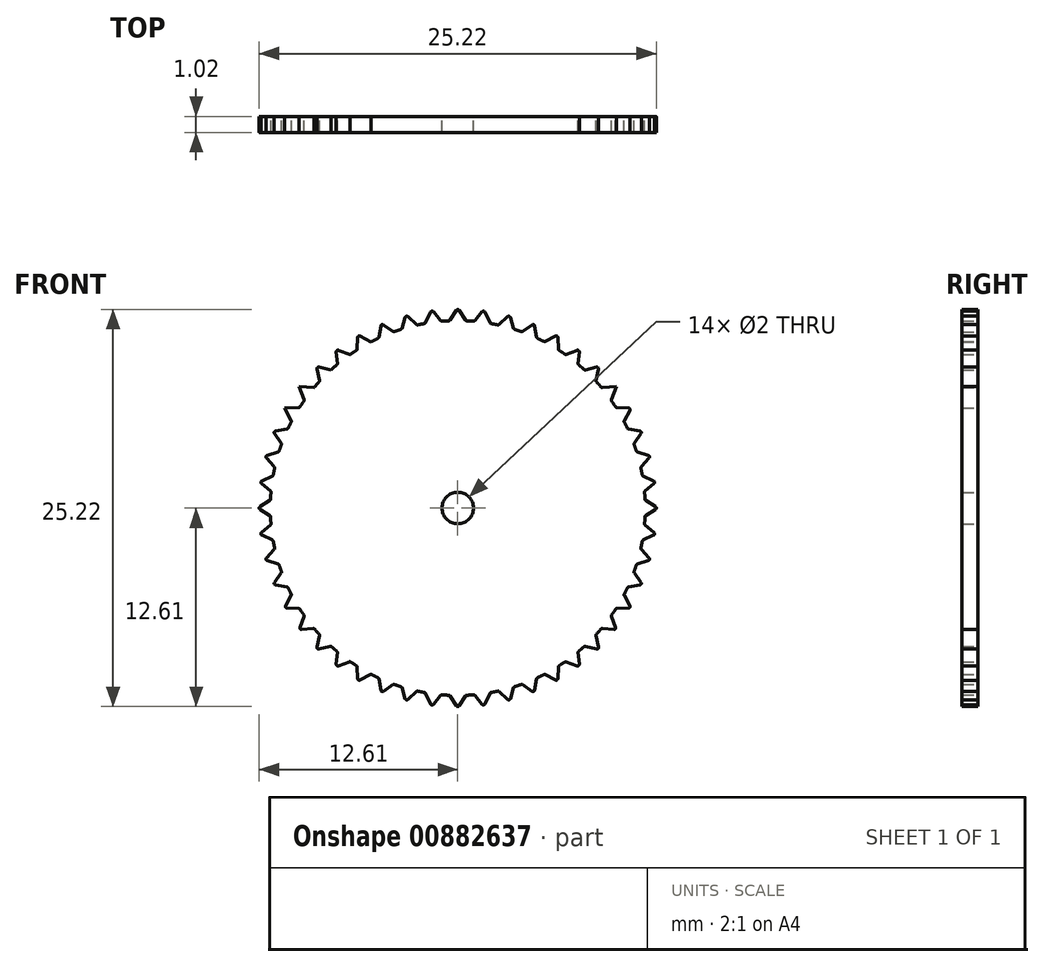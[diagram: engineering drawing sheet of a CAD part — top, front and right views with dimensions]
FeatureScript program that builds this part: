
annotation { "Feature Type Name" : "Feature", "Feature Type Description" : "" }
export const myFeature = defineFeature(function(context is Context, id is Id, definition is map)
    precondition{}
    {
        {
            var Q0;
            Q0=qCreatedBy(makeId("Front.planeOp"),FACE);
            var sketch = newSketch(context, id + "F0", { "sketchPlane" : qUnion([Q0])});
            skArc(sketch, "E0", {"start": v(-0.5, 11.9) * mm, "mid": v(0, -11.9) * mm, "end": v(0.5, 11.9) * mm});
            skLineSegment(sketch, "E1", {"start": v(-0.5, 11.9) * mm, "end": v(0, 12.7) * mm});
            skLineSegment(sketch, "E2", {"start": v(0, 12.7) * mm, "end": v(0.5, 11.9) * mm});
            skPoint(sketch, "E3.start.orphan", {"position": v(-0.5, 15.6) * mm});
            skPoint(sketch, "E4.end.orphan", {"position": v(0, 15.6) * mm});
            skCircle(sketch, "E5", {"center": v(0, 0) * mm, "radius": 1 * mm});
            skPoint(sketch, "E6.end.orphan", {"position": v(0, 11.9) * mm});
            skLineSegment(sketch, "E7.1.0", {"start": v(-2.06, 11.73) * mm, "end": v(-1.66, 12.6) * mm});
            skLineSegment(sketch, "E7.1.1", {"start": v(-1.66, 12.6) * mm, "end": v(-1.05, 11.86) * mm});
            skLineSegment(sketch, "E7.2.0", {"start": v(-3.57, 11.36) * mm, "end": v(-3.29, 12.27) * mm});
            skLineSegment(sketch, "E7.2.1", {"start": v(-3.29, 12.27) * mm, "end": v(-2.59, 11.62) * mm});
            skLineSegment(sketch, "E7.3.0", {"start": v(-5.02, 10.8) * mm, "end": v(-4.86, 11.73) * mm});
            skLineSegment(sketch, "E7.3.1", {"start": v(-4.86, 11.73) * mm, "end": v(-4.08, 11.18) * mm});
            skLineSegment(sketch, "E7.4.0", {"start": v(-6.39, 10.05) * mm, "end": v(-6.35, 11) * mm});
            skLineSegment(sketch, "E7.4.1", {"start": v(-6.35, 11) * mm, "end": v(-5.5, 10.56) * mm});
            skLineSegment(sketch, "E7.5.0", {"start": v(-7.64, 9.13) * mm, "end": v(-7.73, 10.08) * mm});
            skLineSegment(sketch, "E7.5.1", {"start": v(-7.73, 10.08) * mm, "end": v(-6.84, 9.75) * mm});
            skLineSegment(sketch, "E7.6.0", {"start": v(-8.77, 8.05) * mm, "end": v(-8.98, 8.98) * mm});
            skLineSegment(sketch, "E7.6.1", {"start": v(-8.98, 8.98) * mm, "end": v(-8.05, 8.77) * mm});
            skLineSegment(sketch, "E7.7.0", {"start": v(-9.75, 6.84) * mm, "end": v(-10.08, 7.73) * mm});
            skLineSegment(sketch, "E7.7.1", {"start": v(-10.08, 7.73) * mm, "end": v(-9.13, 7.64) * mm});
            skLineSegment(sketch, "E7.8.0", {"start": v(-10.56, 5.5) * mm, "end": v(-11, 6.35) * mm});
            skLineSegment(sketch, "E7.8.1", {"start": v(-11, 6.35) * mm, "end": v(-10.05, 6.39) * mm});
            skLineSegment(sketch, "E7.9.0", {"start": v(-11.18, 4.08) * mm, "end": v(-11.73, 4.86) * mm});
            skLineSegment(sketch, "E7.9.1", {"start": v(-11.73, 4.86) * mm, "end": v(-10.8, 5.02) * mm});
            skLineSegment(sketch, "E7.10.0", {"start": v(-11.62, 2.59) * mm, "end": v(-12.27, 3.29) * mm});
            skLineSegment(sketch, "E7.10.1", {"start": v(-12.27, 3.29) * mm, "end": v(-11.36, 3.57) * mm});
            skLineSegment(sketch, "E7.11.0", {"start": v(-11.86, 1.05) * mm, "end": v(-12.6, 1.66) * mm});
            skLineSegment(sketch, "E7.11.1", {"start": v(-12.6, 1.66) * mm, "end": v(-11.73, 2.06) * mm});
            skLineSegment(sketch, "E7.12.0", {"start": v(-11.9, -0.5) * mm, "end": v(-12.7, 0) * mm});
            skLineSegment(sketch, "E7.12.1", {"start": v(-12.7, 0) * mm, "end": v(-11.9, 0.5) * mm});
            skLineSegment(sketch, "E7.13.0", {"start": v(-11.73, -2.06) * mm, "end": v(-12.6, -1.66) * mm});
            skLineSegment(sketch, "E7.13.1", {"start": v(-12.6, -1.66) * mm, "end": v(-11.86, -1.05) * mm});
            skLineSegment(sketch, "E7.14.0", {"start": v(-11.36, -3.57) * mm, "end": v(-12.27, -3.29) * mm});
            skLineSegment(sketch, "E7.14.1", {"start": v(-12.27, -3.29) * mm, "end": v(-11.62, -2.59) * mm});
            skLineSegment(sketch, "E7.15.0", {"start": v(-10.8, -5.02) * mm, "end": v(-11.73, -4.86) * mm});
            skLineSegment(sketch, "E7.15.1", {"start": v(-11.73, -4.86) * mm, "end": v(-11.18, -4.08) * mm});
            skLineSegment(sketch, "E7.16.0", {"start": v(-10.05, -6.39) * mm, "end": v(-11, -6.35) * mm});
            skLineSegment(sketch, "E7.16.1", {"start": v(-11, -6.35) * mm, "end": v(-10.56, -5.5) * mm});
            skLineSegment(sketch, "E7.17.0", {"start": v(-9.13, -7.64) * mm, "end": v(-10.08, -7.73) * mm});
            skLineSegment(sketch, "E7.17.1", {"start": v(-10.08, -7.73) * mm, "end": v(-9.75, -6.84) * mm});
            skLineSegment(sketch, "E7.18.0", {"start": v(-8.05, -8.77) * mm, "end": v(-8.98, -8.98) * mm});
            skLineSegment(sketch, "E7.18.1", {"start": v(-8.98, -8.98) * mm, "end": v(-8.77, -8.05) * mm});
            skLineSegment(sketch, "E7.19.0", {"start": v(-6.84, -9.75) * mm, "end": v(-7.73, -10.08) * mm});
            skLineSegment(sketch, "E7.19.1", {"start": v(-7.73, -10.08) * mm, "end": v(-7.64, -9.13) * mm});
            skLineSegment(sketch, "E7.20.0", {"start": v(-5.5, -10.56) * mm, "end": v(-6.35, -11) * mm});
            skLineSegment(sketch, "E7.20.1", {"start": v(-6.35, -11) * mm, "end": v(-6.39, -10.05) * mm});
            skLineSegment(sketch, "E7.21.0", {"start": v(-4.08, -11.18) * mm, "end": v(-4.86, -11.73) * mm});
            skLineSegment(sketch, "E7.21.1", {"start": v(-4.86, -11.73) * mm, "end": v(-5.02, -10.8) * mm});
            skLineSegment(sketch, "E7.22.0", {"start": v(-2.59, -11.62) * mm, "end": v(-3.29, -12.27) * mm});
            skLineSegment(sketch, "E7.22.1", {"start": v(-3.29, -12.27) * mm, "end": v(-3.57, -11.36) * mm});
            skLineSegment(sketch, "E7.23.0", {"start": v(-1.05, -11.86) * mm, "end": v(-1.66, -12.6) * mm});
            skLineSegment(sketch, "E7.23.1", {"start": v(-1.66, -12.6) * mm, "end": v(-2.06, -11.73) * mm});
            skLineSegment(sketch, "E7.24.0", {"start": v(0.5, -11.9) * mm, "end": v(0, -12.7) * mm});
            skLineSegment(sketch, "E7.24.1", {"start": v(0, -12.7) * mm, "end": v(-0.5, -11.9) * mm});
            skLineSegment(sketch, "E7.25.0", {"start": v(2.06, -11.73) * mm, "end": v(1.66, -12.6) * mm});
            skLineSegment(sketch, "E7.25.1", {"start": v(1.66, -12.6) * mm, "end": v(1.05, -11.86) * mm});
            skLineSegment(sketch, "E7.26.0", {"start": v(3.57, -11.36) * mm, "end": v(3.29, -12.27) * mm});
            skLineSegment(sketch, "E7.26.1", {"start": v(3.29, -12.27) * mm, "end": v(2.59, -11.62) * mm});
            skLineSegment(sketch, "E7.27.0", {"start": v(5.02, -10.8) * mm, "end": v(4.86, -11.73) * mm});
            skLineSegment(sketch, "E7.27.1", {"start": v(4.86, -11.73) * mm, "end": v(4.08, -11.18) * mm});
            skLineSegment(sketch, "E7.28.0", {"start": v(6.39, -10.05) * mm, "end": v(6.35, -11) * mm});
            skLineSegment(sketch, "E7.28.1", {"start": v(6.35, -11) * mm, "end": v(5.5, -10.56) * mm});
            skLineSegment(sketch, "E7.29.0", {"start": v(7.64, -9.13) * mm, "end": v(7.73, -10.08) * mm});
            skLineSegment(sketch, "E7.29.1", {"start": v(7.73, -10.08) * mm, "end": v(6.84, -9.75) * mm});
            skLineSegment(sketch, "E7.30.0", {"start": v(8.77, -8.05) * mm, "end": v(8.98, -8.98) * mm});
            skLineSegment(sketch, "E7.30.1", {"start": v(8.98, -8.98) * mm, "end": v(8.05, -8.77) * mm});
            skLineSegment(sketch, "E7.31.0", {"start": v(9.75, -6.84) * mm, "end": v(10.08, -7.73) * mm});
            skLineSegment(sketch, "E7.31.1", {"start": v(10.08, -7.73) * mm, "end": v(9.13, -7.64) * mm});
            skLineSegment(sketch, "E7.32.0", {"start": v(10.56, -5.5) * mm, "end": v(11, -6.35) * mm});
            skLineSegment(sketch, "E7.32.1", {"start": v(11, -6.35) * mm, "end": v(10.05, -6.39) * mm});
            skLineSegment(sketch, "E7.33.0", {"start": v(11.18, -4.08) * mm, "end": v(11.73, -4.86) * mm});
            skLineSegment(sketch, "E7.33.1", {"start": v(11.73, -4.86) * mm, "end": v(10.8, -5.02) * mm});
            skLineSegment(sketch, "E7.34.0", {"start": v(11.62, -2.59) * mm, "end": v(12.27, -3.29) * mm});
            skLineSegment(sketch, "E7.34.1", {"start": v(12.27, -3.29) * mm, "end": v(11.36, -3.57) * mm});
            skLineSegment(sketch, "E7.35.0", {"start": v(11.86, -1.05) * mm, "end": v(12.6, -1.66) * mm});
            skLineSegment(sketch, "E7.35.1", {"start": v(12.6, -1.66) * mm, "end": v(11.73, -2.06) * mm});
            skLineSegment(sketch, "E7.36.0", {"start": v(11.9, 0.5) * mm, "end": v(12.7, 0) * mm});
            skLineSegment(sketch, "E7.36.1", {"start": v(12.7, 0) * mm, "end": v(11.9, -0.5) * mm});
            skLineSegment(sketch, "E7.37.0", {"start": v(11.73, 2.06) * mm, "end": v(12.6, 1.66) * mm});
            skLineSegment(sketch, "E7.37.1", {"start": v(12.6, 1.66) * mm, "end": v(11.86, 1.05) * mm});
            skLineSegment(sketch, "E7.38.0", {"start": v(11.36, 3.57) * mm, "end": v(12.27, 3.29) * mm});
            skLineSegment(sketch, "E7.38.1", {"start": v(12.27, 3.29) * mm, "end": v(11.62, 2.59) * mm});
            skLineSegment(sketch, "E7.39.0", {"start": v(10.8, 5.02) * mm, "end": v(11.73, 4.86) * mm});
            skLineSegment(sketch, "E7.39.1", {"start": v(11.73, 4.86) * mm, "end": v(11.18, 4.08) * mm});
            skLineSegment(sketch, "E7.40.0", {"start": v(10.05, 6.39) * mm, "end": v(11, 6.35) * mm});
            skLineSegment(sketch, "E7.40.1", {"start": v(11, 6.35) * mm, "end": v(10.56, 5.5) * mm});
            skLineSegment(sketch, "E7.41.0", {"start": v(9.13, 7.64) * mm, "end": v(10.08, 7.73) * mm});
            skLineSegment(sketch, "E7.41.1", {"start": v(10.08, 7.73) * mm, "end": v(9.75, 6.84) * mm});
            skLineSegment(sketch, "E7.42.0", {"start": v(8.05, 8.77) * mm, "end": v(8.98, 8.98) * mm});
            skLineSegment(sketch, "E7.42.1", {"start": v(8.98, 8.98) * mm, "end": v(8.77, 8.05) * mm});
            skLineSegment(sketch, "E7.43.0", {"start": v(6.84, 9.75) * mm, "end": v(7.73, 10.08) * mm});
            skLineSegment(sketch, "E7.43.1", {"start": v(7.73, 10.08) * mm, "end": v(7.64, 9.13) * mm});
            skLineSegment(sketch, "E7.44.0", {"start": v(5.5, 10.56) * mm, "end": v(6.35, 11) * mm});
            skLineSegment(sketch, "E7.44.1", {"start": v(6.35, 11) * mm, "end": v(6.39, 10.05) * mm});
            skLineSegment(sketch, "E7.45.0", {"start": v(4.08, 11.18) * mm, "end": v(4.86, 11.73) * mm});
            skLineSegment(sketch, "E7.45.1", {"start": v(4.86, 11.73) * mm, "end": v(5.02, 10.8) * mm});
            skLineSegment(sketch, "E7.46.0", {"start": v(2.59, 11.62) * mm, "end": v(3.29, 12.27) * mm});
            skLineSegment(sketch, "E7.46.1", {"start": v(3.29, 12.27) * mm, "end": v(3.57, 11.36) * mm});
            skLineSegment(sketch, "E7.47.0", {"start": v(1.05, 11.86) * mm, "end": v(1.66, 12.6) * mm});
            skLineSegment(sketch, "E7.47.1", {"start": v(1.66, 12.6) * mm, "end": v(2.06, 11.73) * mm});
            skSolve(sketch);
        }
        {
            var Q0;
            {var subQ0=sQuery(id+"F0.wireOp",EDGE,"E1");Q0=makeQuery(id+"F0.imprint","IMPRINT",FACE,{"disambiguationData":[TD([[makeQuery(id+"F0.imprint","IMPRINT",EDGE,{"derivedFrom":subQ0}),-1.0]])]});}
            var Q1;
            {var subQ0=sQuery(id+"F0.wireOp",EDGE,"E7.1.0");Q1=makeQuery(id+"F0.imprint","IMPRINT",FACE,{"disambiguationData":[TD([[makeQuery(id+"F0.imprint","IMPRINT",EDGE,{"derivedFrom":subQ0}),-1.0]])]});}
            var Q2;
            {var subQ0=sQuery(id+"F0.wireOp",EDGE,"E7.2.0");Q2=makeQuery(id+"F0.imprint","IMPRINT",FACE,{"disambiguationData":[TD([[makeQuery(id+"F0.imprint","IMPRINT",EDGE,{"derivedFrom":subQ0}),-1.0]])]});}
            var Q3;
            {var subQ0=sQuery(id+"F0.wireOp",EDGE,"E7.3.0");Q3=makeQuery(id+"F0.imprint","IMPRINT",FACE,{"disambiguationData":[TD([[makeQuery(id+"F0.imprint","IMPRINT",EDGE,{"derivedFrom":subQ0}),-1.0]])]});}
            var Q4;
            {var subQ0=sQuery(id+"F0.wireOp",EDGE,"E7.4.0");Q4=makeQuery(id+"F0.imprint","IMPRINT",FACE,{"disambiguationData":[TD([[makeQuery(id+"F0.imprint","IMPRINT",EDGE,{"derivedFrom":subQ0}),-1.0]])]});}
            var Q5;
            {var subQ0=sQuery(id+"F0.wireOp",EDGE,"E7.5.0");Q5=makeQuery(id+"F0.imprint","IMPRINT",FACE,{"disambiguationData":[TD([[makeQuery(id+"F0.imprint","IMPRINT",EDGE,{"derivedFrom":subQ0}),-1.0]])]});}
            var Q6;
            {var subQ0=sQuery(id+"F0.wireOp",EDGE,"E7.6.0");Q6=makeQuery(id+"F0.imprint","IMPRINT",FACE,{"disambiguationData":[TD([[makeQuery(id+"F0.imprint","IMPRINT",EDGE,{"derivedFrom":subQ0}),-1.0]])]});}
            var Q7;
            {var subQ0=sQuery(id+"F0.wireOp",EDGE,"E7.8.0");Q7=makeQuery(id+"F0.imprint","IMPRINT",FACE,{"disambiguationData":[TD([[makeQuery(id+"F0.imprint","IMPRINT",EDGE,{"derivedFrom":subQ0}),-1.0]])]});}
            var Q8;
            {var subQ0=sQuery(id+"F0.wireOp",EDGE,"E7.9.0");Q8=makeQuery(id+"F0.imprint","IMPRINT",FACE,{"disambiguationData":[TD([[makeQuery(id+"F0.imprint","IMPRINT",EDGE,{"derivedFrom":subQ0}),-1.0]])]});}
            var Q9;
            {var subQ0=sQuery(id+"F0.wireOp",EDGE,"E7.10.0");Q9=makeQuery(id+"F0.imprint","IMPRINT",FACE,{"disambiguationData":[TD([[makeQuery(id+"F0.imprint","IMPRINT",EDGE,{"derivedFrom":subQ0}),-1.0]])]});}
            var Q10;
            {var subQ0=sQuery(id+"F0.wireOp",EDGE,"E7.11.0");Q10=makeQuery(id+"F0.imprint","IMPRINT",FACE,{"disambiguationData":[TD([[makeQuery(id+"F0.imprint","IMPRINT",EDGE,{"derivedFrom":subQ0}),-1.0]])]});}
            var Q11;
            {var subQ0=sQuery(id+"F0.wireOp",EDGE,"E7.12.0");Q11=makeQuery(id+"F0.imprint","IMPRINT",FACE,{"disambiguationData":[TD([[makeQuery(id+"F0.imprint","IMPRINT",EDGE,{"derivedFrom":subQ0}),-1.0]])]});}
            var Q12;
            {var subQ0=sQuery(id+"F0.wireOp",EDGE,"E7.13.0");Q12=makeQuery(id+"F0.imprint","IMPRINT",FACE,{"disambiguationData":[TD([[makeQuery(id+"F0.imprint","IMPRINT",EDGE,{"derivedFrom":subQ0}),-1.0]])]});}
            var Q13;
            {var subQ0=sQuery(id+"F0.wireOp",EDGE,"E7.7.0");Q13=makeQuery(id+"F0.imprint","IMPRINT",FACE,{"disambiguationData":[TD([[makeQuery(id+"F0.imprint","IMPRINT",EDGE,{"derivedFrom":subQ0}),-1.0]])]});}
            var Q14;
            {var subQ0=sQuery(id+"F0.wireOp",EDGE,"E7.14.0");Q14=makeQuery(id+"F0.imprint","IMPRINT",FACE,{"disambiguationData":[TD([[makeQuery(id+"F0.imprint","IMPRINT",EDGE,{"derivedFrom":subQ0}),-1.0]])]});}
            var Q15;
            {var subQ0=sQuery(id+"F0.wireOp",EDGE,"E7.15.0");Q15=makeQuery(id+"F0.imprint","IMPRINT",FACE,{"disambiguationData":[TD([[makeQuery(id+"F0.imprint","IMPRINT",EDGE,{"derivedFrom":subQ0}),-1.0]])]});}
            var Q16;
            {var subQ0=sQuery(id+"F0.wireOp",EDGE,"E7.16.0");Q16=makeQuery(id+"F0.imprint","IMPRINT",FACE,{"disambiguationData":[TD([[makeQuery(id+"F0.imprint","IMPRINT",EDGE,{"derivedFrom":subQ0}),-1.0]])]});}
            var Q17;
            {var subQ0=sQuery(id+"F0.wireOp",EDGE,"E7.47.0");Q17=makeQuery(id+"F0.imprint","IMPRINT",FACE,{"disambiguationData":[TD([[makeQuery(id+"F0.imprint","IMPRINT",EDGE,{"derivedFrom":subQ0}),-1.0]])]});}
            var Q18;
            {var subQ0=sQuery(id+"F0.wireOp",EDGE,"E7.46.0");Q18=makeQuery(id+"F0.imprint","IMPRINT",FACE,{"disambiguationData":[TD([[makeQuery(id+"F0.imprint","IMPRINT",EDGE,{"derivedFrom":subQ0}),-1.0]])]});}
            var Q19;
            {var subQ0=sQuery(id+"F0.wireOp",EDGE,"E7.45.0");Q19=makeQuery(id+"F0.imprint","IMPRINT",FACE,{"disambiguationData":[TD([[makeQuery(id+"F0.imprint","IMPRINT",EDGE,{"derivedFrom":subQ0}),-1.0]])]});}
            var Q20;
            {var subQ0=sQuery(id+"F0.wireOp",EDGE,"E7.44.0");Q20=makeQuery(id+"F0.imprint","IMPRINT",FACE,{"disambiguationData":[TD([[makeQuery(id+"F0.imprint","IMPRINT",EDGE,{"derivedFrom":subQ0}),-1.0]])]});}
            var Q21;
            {var subQ0=sQuery(id+"F0.wireOp",EDGE,"E7.43.0");Q21=makeQuery(id+"F0.imprint","IMPRINT",FACE,{"disambiguationData":[TD([[makeQuery(id+"F0.imprint","IMPRINT",EDGE,{"derivedFrom":subQ0}),-1.0]])]});}
            var Q22;
            {var subQ0=sQuery(id+"F0.wireOp",EDGE,"E7.42.0");Q22=makeQuery(id+"F0.imprint","IMPRINT",FACE,{"disambiguationData":[TD([[makeQuery(id+"F0.imprint","IMPRINT",EDGE,{"derivedFrom":subQ0}),-1.0]])]});}
            var Q23;
            {var subQ0=sQuery(id+"F0.wireOp",EDGE,"E7.41.0");Q23=makeQuery(id+"F0.imprint","IMPRINT",FACE,{"disambiguationData":[TD([[makeQuery(id+"F0.imprint","IMPRINT",EDGE,{"derivedFrom":subQ0}),-1.0]])]});}
            var Q24;
            {var subQ0=sQuery(id+"F0.wireOp",EDGE,"E7.40.0");Q24=makeQuery(id+"F0.imprint","IMPRINT",FACE,{"disambiguationData":[TD([[makeQuery(id+"F0.imprint","IMPRINT",EDGE,{"derivedFrom":subQ0}),-1.0]])]});}
            var Q25;
            {var subQ0=sQuery(id+"F0.wireOp",EDGE,"E7.39.0");Q25=makeQuery(id+"F0.imprint","IMPRINT",FACE,{"disambiguationData":[TD([[makeQuery(id+"F0.imprint","IMPRINT",EDGE,{"derivedFrom":subQ0}),-1.0]])]});}
            var Q26;
            {var subQ0=sQuery(id+"F0.wireOp",EDGE,"E7.38.0");Q26=makeQuery(id+"F0.imprint","IMPRINT",FACE,{"disambiguationData":[TD([[makeQuery(id+"F0.imprint","IMPRINT",EDGE,{"derivedFrom":subQ0}),-1.0]])]});}
            var Q27;
            {var subQ0=sQuery(id+"F0.wireOp",EDGE,"E7.37.0");Q27=makeQuery(id+"F0.imprint","IMPRINT",FACE,{"disambiguationData":[TD([[makeQuery(id+"F0.imprint","IMPRINT",EDGE,{"derivedFrom":subQ0}),-1.0]])]});}
            var Q28;
            {var subQ0=sQuery(id+"F0.wireOp",EDGE,"E7.36.0");Q28=makeQuery(id+"F0.imprint","IMPRINT",FACE,{"disambiguationData":[TD([[makeQuery(id+"F0.imprint","IMPRINT",EDGE,{"derivedFrom":subQ0}),-1.0]])]});}
            var Q29;
            {var subQ0=sQuery(id+"F0.wireOp",EDGE,"E7.35.0");Q29=makeQuery(id+"F0.imprint","IMPRINT",FACE,{"disambiguationData":[TD([[makeQuery(id+"F0.imprint","IMPRINT",EDGE,{"derivedFrom":subQ0}),-1.0]])]});}
            var Q30;
            {var subQ0=sQuery(id+"F0.wireOp",EDGE,"E7.34.0");Q30=makeQuery(id+"F0.imprint","IMPRINT",FACE,{"disambiguationData":[TD([[makeQuery(id+"F0.imprint","IMPRINT",EDGE,{"derivedFrom":subQ0}),-1.0]])]});}
            var Q31;
            {var subQ0=sQuery(id+"F0.wireOp",EDGE,"E7.33.0");Q31=makeQuery(id+"F0.imprint","IMPRINT",FACE,{"disambiguationData":[TD([[makeQuery(id+"F0.imprint","IMPRINT",EDGE,{"derivedFrom":subQ0}),-1.0]])]});}
            var Q32;
            {var subQ0=sQuery(id+"F0.wireOp",EDGE,"E7.32.0");Q32=makeQuery(id+"F0.imprint","IMPRINT",FACE,{"disambiguationData":[TD([[makeQuery(id+"F0.imprint","IMPRINT",EDGE,{"derivedFrom":subQ0}),-1.0]])]});}
            var Q33;
            {var subQ0=sQuery(id+"F0.wireOp",EDGE,"E7.31.0");Q33=makeQuery(id+"F0.imprint","IMPRINT",FACE,{"disambiguationData":[TD([[makeQuery(id+"F0.imprint","IMPRINT",EDGE,{"derivedFrom":subQ0}),-1.0]])]});}
            var Q34;
            {var subQ0=sQuery(id+"F0.wireOp",EDGE,"E7.30.0");Q34=makeQuery(id+"F0.imprint","IMPRINT",FACE,{"disambiguationData":[TD([[makeQuery(id+"F0.imprint","IMPRINT",EDGE,{"derivedFrom":subQ0}),-1.0]])]});}
            var Q35;
            {var subQ0=sQuery(id+"F0.wireOp",EDGE,"E7.29.0");Q35=makeQuery(id+"F0.imprint","IMPRINT",FACE,{"disambiguationData":[TD([[makeQuery(id+"F0.imprint","IMPRINT",EDGE,{"derivedFrom":subQ0}),-1.0]])]});}
            var Q36;
            {var subQ0=sQuery(id+"F0.wireOp",EDGE,"E7.28.0");Q36=makeQuery(id+"F0.imprint","IMPRINT",FACE,{"disambiguationData":[TD([[makeQuery(id+"F0.imprint","IMPRINT",EDGE,{"derivedFrom":subQ0}),-1.0]])]});}
            var Q37;
            {var subQ0=sQuery(id+"F0.wireOp",EDGE,"E7.27.0");Q37=makeQuery(id+"F0.imprint","IMPRINT",FACE,{"disambiguationData":[TD([[makeQuery(id+"F0.imprint","IMPRINT",EDGE,{"derivedFrom":subQ0}),-1.0]])]});}
            var Q38;
            {var subQ0=sQuery(id+"F0.wireOp",EDGE,"E7.26.0");Q38=makeQuery(id+"F0.imprint","IMPRINT",FACE,{"disambiguationData":[TD([[makeQuery(id+"F0.imprint","IMPRINT",EDGE,{"derivedFrom":subQ0}),-1.0]])]});}
            var Q39;
            {var subQ0=sQuery(id+"F0.wireOp",EDGE,"E7.25.0");Q39=makeQuery(id+"F0.imprint","IMPRINT",FACE,{"disambiguationData":[TD([[makeQuery(id+"F0.imprint","IMPRINT",EDGE,{"derivedFrom":subQ0}),-1.0]])]});}
            var Q40;
            {var subQ0=sQuery(id+"F0.wireOp",EDGE,"E7.24.0");Q40=makeQuery(id+"F0.imprint","IMPRINT",FACE,{"disambiguationData":[TD([[makeQuery(id+"F0.imprint","IMPRINT",EDGE,{"derivedFrom":subQ0}),-1.0]])]});}
            var Q41;
            {var subQ0=sQuery(id+"F0.wireOp",EDGE,"E7.23.0");Q41=makeQuery(id+"F0.imprint","IMPRINT",FACE,{"disambiguationData":[TD([[makeQuery(id+"F0.imprint","IMPRINT",EDGE,{"derivedFrom":subQ0}),-1.0]])]});}
            var Q42;
            {var subQ0=sQuery(id+"F0.wireOp",EDGE,"E7.22.0");Q42=makeQuery(id+"F0.imprint","IMPRINT",FACE,{"disambiguationData":[TD([[makeQuery(id+"F0.imprint","IMPRINT",EDGE,{"derivedFrom":subQ0}),-1.0]])]});}
            var Q43;
            {var subQ0=sQuery(id+"F0.wireOp",EDGE,"E7.21.0");Q43=makeQuery(id+"F0.imprint","IMPRINT",FACE,{"disambiguationData":[TD([[makeQuery(id+"F0.imprint","IMPRINT",EDGE,{"derivedFrom":subQ0}),-1.0]])]});}
            var Q44;
            {var subQ0=sQuery(id+"F0.wireOp",EDGE,"E7.20.0");Q44=makeQuery(id+"F0.imprint","IMPRINT",FACE,{"disambiguationData":[TD([[makeQuery(id+"F0.imprint","IMPRINT",EDGE,{"derivedFrom":subQ0}),-1.0]])]});}
            var Q45;
            {var subQ0=sQuery(id+"F0.wireOp",EDGE,"E7.19.0");Q45=makeQuery(id+"F0.imprint","IMPRINT",FACE,{"disambiguationData":[TD([[makeQuery(id+"F0.imprint","IMPRINT",EDGE,{"derivedFrom":subQ0}),-1.0]])]});}
            var Q46;
            {var subQ0=sQuery(id+"F0.wireOp",EDGE,"E7.18.0");Q46=makeQuery(id+"F0.imprint","IMPRINT",FACE,{"disambiguationData":[TD([[makeQuery(id+"F0.imprint","IMPRINT",EDGE,{"derivedFrom":subQ0}),-1.0]])]});}
            var Q47;
            {var subQ0=sQuery(id+"F0.wireOp",EDGE,"E7.17.0");Q47=makeQuery(id+"F0.imprint","IMPRINT",FACE,{"disambiguationData":[TD([[makeQuery(id+"F0.imprint","IMPRINT",EDGE,{"derivedFrom":subQ0}),-1.0]])]});}
            extrude(context, id + "F1", {"entities" : qUnion([Q0, Q1, Q2, Q3, Q4, Q5, Q6, Q7, Q8, Q9, Q10, Q11, Q12, Q13, Q14, Q15, Q16, Q17, Q18, Q19, Q20, Q21, Q22, Q23, Q24, Q25, Q26, Q27, Q28, Q29, Q30, Q31, Q32, Q33, Q34, Q35, Q36, Q37, Q38, Q39, Q40, Q41, Q42, Q43, Q44, Q45, Q46, Q47]), "depth" : 1.02 * mm, "offsetDistance" : 25.4 * mm});
        }
        {
            var Q0;
            Q0=makeQuery(id+"F1.opExtrude","SWEPT_EDGE",EDGE,{"disambiguationData":[OSD([sQuery(id+"F0.wireOp",EDGE,"E7.1.0"),sQuery(id+"F0.wireOp",EDGE,"E7.1.1")])]});
            var Q1;
            Q1=makeQuery(id+"F1.opExtrude","SWEPT_EDGE",EDGE,{"disambiguationData":[OSD([sQuery(id+"F0.wireOp",EDGE,"E0"),sQuery(id+"F0.wireOp",EDGE,"E7.1.1")])]});
            var Q2;
            Q2=makeQuery(id+"F1.opExtrude","SWEPT_EDGE",EDGE,{"disambiguationData":[OSD([sQuery(id+"F0.wireOp",EDGE,"E0"),sQuery(id+"F0.wireOp",EDGE,"E1")])]});
            var Q3;
            Q3=makeQuery(id+"F1.opExtrude","SWEPT_EDGE",EDGE,{"disambiguationData":[OSD([sQuery(id+"F0.wireOp",EDGE,"E1"),sQuery(id+"F0.wireOp",EDGE,"E2")])]});
            var Q4;
            Q4=makeQuery(id+"F1.opExtrude","SWEPT_EDGE",EDGE,{"disambiguationData":[OSD([sQuery(id+"F0.wireOp",EDGE,"E0"),sQuery(id+"F0.wireOp",EDGE,"E2")])]});
            var Q5;
            Q5=makeQuery(id+"F1.opExtrude","SWEPT_EDGE",EDGE,{"disambiguationData":[OSD([sQuery(id+"F0.wireOp",EDGE,"E0"),sQuery(id+"F0.wireOp",EDGE,"E7.47.0")])]});
            var Q6;
            Q6=makeQuery(id+"F1.opExtrude","SWEPT_EDGE",EDGE,{"disambiguationData":[OSD([sQuery(id+"F0.wireOp",EDGE,"E7.47.0"),sQuery(id+"F0.wireOp",EDGE,"E7.47.1")])]});
            var Q7;
            Q7=makeQuery(id+"F1.opExtrude","SWEPT_EDGE",EDGE,{"disambiguationData":[OSD([sQuery(id+"F0.wireOp",EDGE,"E0"),sQuery(id+"F0.wireOp",EDGE,"E7.47.1")])]});
            var Q8;
            Q8=makeQuery(id+"F1.opExtrude","SWEPT_EDGE",EDGE,{"disambiguationData":[OSD([sQuery(id+"F0.wireOp",EDGE,"E0"),sQuery(id+"F0.wireOp",EDGE,"E7.46.0")])]});
            var Q9;
            Q9=makeQuery(id+"F1.opExtrude","SWEPT_EDGE",EDGE,{"disambiguationData":[OSD([sQuery(id+"F0.wireOp",EDGE,"E7.46.0"),sQuery(id+"F0.wireOp",EDGE,"E7.46.1")])]});
            var Q10;
            Q10=makeQuery(id+"F1.opExtrude","SWEPT_EDGE",EDGE,{"disambiguationData":[OSD([sQuery(id+"F0.wireOp",EDGE,"E0"),sQuery(id+"F0.wireOp",EDGE,"E7.46.1")])]});
            var Q11;
            Q11=makeQuery(id+"F1.opExtrude","SWEPT_EDGE",EDGE,{"disambiguationData":[OSD([sQuery(id+"F0.wireOp",EDGE,"E0"),sQuery(id+"F0.wireOp",EDGE,"E7.45.0")])]});
            var Q12;
            Q12=makeQuery(id+"F1.opExtrude","SWEPT_EDGE",EDGE,{"disambiguationData":[OSD([sQuery(id+"F0.wireOp",EDGE,"E7.45.0"),sQuery(id+"F0.wireOp",EDGE,"E7.45.1")])]});
            var Q13;
            Q13=makeQuery(id+"F1.opExtrude","SWEPT_EDGE",EDGE,{"disambiguationData":[OSD([sQuery(id+"F0.wireOp",EDGE,"E0"),sQuery(id+"F0.wireOp",EDGE,"E7.45.1")])]});
            var Q14;
            Q14=makeQuery(id+"F1.opExtrude","SWEPT_EDGE",EDGE,{"disambiguationData":[OSD([sQuery(id+"F0.wireOp",EDGE,"E0"),sQuery(id+"F0.wireOp",EDGE,"E7.44.0")])]});
            var Q15;
            Q15=makeQuery(id+"F1.opExtrude","SWEPT_EDGE",EDGE,{"disambiguationData":[OSD([sQuery(id+"F0.wireOp",EDGE,"E7.44.0"),sQuery(id+"F0.wireOp",EDGE,"E7.44.1")])]});
            var Q16;
            Q16=makeQuery(id+"F1.opExtrude","SWEPT_EDGE",EDGE,{"disambiguationData":[OSD([sQuery(id+"F0.wireOp",EDGE,"E0"),sQuery(id+"F0.wireOp",EDGE,"E7.44.1")])]});
            var Q17;
            Q17=makeQuery(id+"F1.opExtrude","SWEPT_EDGE",EDGE,{"disambiguationData":[OSD([sQuery(id+"F0.wireOp",EDGE,"E0"),sQuery(id+"F0.wireOp",EDGE,"E7.43.0")])]});
            var Q18;
            Q18=makeQuery(id+"F1.opExtrude","SWEPT_EDGE",EDGE,{"disambiguationData":[OSD([sQuery(id+"F0.wireOp",EDGE,"E7.43.0"),sQuery(id+"F0.wireOp",EDGE,"E7.43.1")])]});
            var Q19;
            Q19=makeQuery(id+"F1.opExtrude","SWEPT_EDGE",EDGE,{"disambiguationData":[OSD([sQuery(id+"F0.wireOp",EDGE,"E0"),sQuery(id+"F0.wireOp",EDGE,"E7.43.1")])]});
            var Q20;
            Q20=makeQuery(id+"F1.opExtrude","SWEPT_EDGE",EDGE,{"disambiguationData":[OSD([sQuery(id+"F0.wireOp",EDGE,"E0"),sQuery(id+"F0.wireOp",EDGE,"E7.42.0")])]});
            var Q21;
            Q21=makeQuery(id+"F1.opExtrude","SWEPT_EDGE",EDGE,{"disambiguationData":[OSD([sQuery(id+"F0.wireOp",EDGE,"E7.42.0"),sQuery(id+"F0.wireOp",EDGE,"E7.42.1")])]});
            var Q22;
            Q22=makeQuery(id+"F1.opExtrude","SWEPT_EDGE",EDGE,{"disambiguationData":[OSD([sQuery(id+"F0.wireOp",EDGE,"E0"),sQuery(id+"F0.wireOp",EDGE,"E7.42.1")])]});
            var Q23;
            Q23=makeQuery(id+"F1.opExtrude","SWEPT_EDGE",EDGE,{"disambiguationData":[OSD([sQuery(id+"F0.wireOp",EDGE,"E0"),sQuery(id+"F0.wireOp",EDGE,"E7.41.0")])]});
            var Q24;
            Q24=makeQuery(id+"F1.opExtrude","SWEPT_EDGE",EDGE,{"disambiguationData":[OSD([sQuery(id+"F0.wireOp",EDGE,"E0"),sQuery(id+"F0.wireOp",EDGE,"E7.41.1")])]});
            var Q25;
            Q25=makeQuery(id+"F1.opExtrude","SWEPT_EDGE",EDGE,{"disambiguationData":[OSD([sQuery(id+"F0.wireOp",EDGE,"E0"),sQuery(id+"F0.wireOp",EDGE,"E7.40.0")])]});
            var Q26;
            Q26=makeQuery(id+"F1.opExtrude","SWEPT_EDGE",EDGE,{"disambiguationData":[OSD([sQuery(id+"F0.wireOp",EDGE,"E7.40.0"),sQuery(id+"F0.wireOp",EDGE,"E7.40.1")])]});
            var Q27;
            Q27=makeQuery(id+"F1.opExtrude","SWEPT_EDGE",EDGE,{"disambiguationData":[OSD([sQuery(id+"F0.wireOp",EDGE,"E0"),sQuery(id+"F0.wireOp",EDGE,"E7.40.1")])]});
            var Q28;
            Q28=makeQuery(id+"F1.opExtrude","SWEPT_EDGE",EDGE,{"disambiguationData":[OSD([sQuery(id+"F0.wireOp",EDGE,"E0"),sQuery(id+"F0.wireOp",EDGE,"E7.39.0")])]});
            var Q29;
            Q29=makeQuery(id+"F1.opExtrude","SWEPT_EDGE",EDGE,{"disambiguationData":[OSD([sQuery(id+"F0.wireOp",EDGE,"E7.39.0"),sQuery(id+"F0.wireOp",EDGE,"E7.39.1")])]});
            var Q30;
            Q30=makeQuery(id+"F1.opExtrude","SWEPT_EDGE",EDGE,{"disambiguationData":[OSD([sQuery(id+"F0.wireOp",EDGE,"E0"),sQuery(id+"F0.wireOp",EDGE,"E7.39.1")])]});
            var Q31;
            Q31=makeQuery(id+"F1.opExtrude","SWEPT_EDGE",EDGE,{"disambiguationData":[OSD([sQuery(id+"F0.wireOp",EDGE,"E0"),sQuery(id+"F0.wireOp",EDGE,"E7.38.0")])]});
            var Q32;
            Q32=makeQuery(id+"F1.opExtrude","SWEPT_EDGE",EDGE,{"disambiguationData":[OSD([sQuery(id+"F0.wireOp",EDGE,"E7.38.0"),sQuery(id+"F0.wireOp",EDGE,"E7.38.1")])]});
            var Q33;
            Q33=makeQuery(id+"F1.opExtrude","SWEPT_EDGE",EDGE,{"disambiguationData":[OSD([sQuery(id+"F0.wireOp",EDGE,"E0"),sQuery(id+"F0.wireOp",EDGE,"E7.38.1")])]});
            var Q34;
            Q34=makeQuery(id+"F1.opExtrude","SWEPT_EDGE",EDGE,{"disambiguationData":[OSD([sQuery(id+"F0.wireOp",EDGE,"E0"),sQuery(id+"F0.wireOp",EDGE,"E7.37.0")])]});
            var Q35;
            Q35=makeQuery(id+"F1.opExtrude","SWEPT_EDGE",EDGE,{"disambiguationData":[OSD([sQuery(id+"F0.wireOp",EDGE,"E7.37.0"),sQuery(id+"F0.wireOp",EDGE,"E7.37.1")])]});
            var Q36;
            Q36=makeQuery(id+"F1.opExtrude","SWEPT_EDGE",EDGE,{"disambiguationData":[OSD([sQuery(id+"F0.wireOp",EDGE,"E0"),sQuery(id+"F0.wireOp",EDGE,"E7.37.1")])]});
            var Q37;
            Q37=makeQuery(id+"F1.opExtrude","SWEPT_EDGE",EDGE,{"disambiguationData":[OSD([sQuery(id+"F0.wireOp",EDGE,"E0"),sQuery(id+"F0.wireOp",EDGE,"E7.36.0")])]});
            var Q38;
            Q38=makeQuery(id+"F1.opExtrude","SWEPT_EDGE",EDGE,{"disambiguationData":[OSD([sQuery(id+"F0.wireOp",EDGE,"E7.36.0"),sQuery(id+"F0.wireOp",EDGE,"E7.36.1")])]});
            var Q39;
            Q39=makeQuery(id+"F1.opExtrude","SWEPT_EDGE",EDGE,{"disambiguationData":[OSD([sQuery(id+"F0.wireOp",EDGE,"E0"),sQuery(id+"F0.wireOp",EDGE,"E7.36.1")])]});
            var Q40;
            Q40=makeQuery(id+"F1.opExtrude","SWEPT_EDGE",EDGE,{"disambiguationData":[OSD([sQuery(id+"F0.wireOp",EDGE,"E0"),sQuery(id+"F0.wireOp",EDGE,"E7.35.0")])]});
            var Q41;
            Q41=makeQuery(id+"F1.opExtrude","SWEPT_EDGE",EDGE,{"disambiguationData":[OSD([sQuery(id+"F0.wireOp",EDGE,"E7.35.0"),sQuery(id+"F0.wireOp",EDGE,"E7.35.1")])]});
            var Q42;
            Q42=makeQuery(id+"F1.opExtrude","SWEPT_EDGE",EDGE,{"disambiguationData":[OSD([sQuery(id+"F0.wireOp",EDGE,"E0"),sQuery(id+"F0.wireOp",EDGE,"E7.35.1")])]});
            var Q43;
            Q43=makeQuery(id+"F1.opExtrude","SWEPT_EDGE",EDGE,{"disambiguationData":[OSD([sQuery(id+"F0.wireOp",EDGE,"E0"),sQuery(id+"F0.wireOp",EDGE,"E7.34.0")])]});
            var Q44;
            Q44=makeQuery(id+"F1.opExtrude","SWEPT_EDGE",EDGE,{"disambiguationData":[OSD([sQuery(id+"F0.wireOp",EDGE,"E7.34.0"),sQuery(id+"F0.wireOp",EDGE,"E7.34.1")])]});
            var Q45;
            Q45=makeQuery(id+"F1.opExtrude","SWEPT_EDGE",EDGE,{"disambiguationData":[OSD([sQuery(id+"F0.wireOp",EDGE,"E0"),sQuery(id+"F0.wireOp",EDGE,"E7.34.1")])]});
            var Q46;
            Q46=makeQuery(id+"F1.opExtrude","SWEPT_EDGE",EDGE,{"disambiguationData":[OSD([sQuery(id+"F0.wireOp",EDGE,"E0"),sQuery(id+"F0.wireOp",EDGE,"E7.33.0")])]});
            var Q47;
            Q47=makeQuery(id+"F1.opExtrude","SWEPT_EDGE",EDGE,{"disambiguationData":[OSD([sQuery(id+"F0.wireOp",EDGE,"E7.33.0"),sQuery(id+"F0.wireOp",EDGE,"E7.33.1")])]});
            var Q48;
            Q48=makeQuery(id+"F1.opExtrude","SWEPT_EDGE",EDGE,{"disambiguationData":[OSD([sQuery(id+"F0.wireOp",EDGE,"E0"),sQuery(id+"F0.wireOp",EDGE,"E7.32.0")])]});
            var Q49;
            Q49=makeQuery(id+"F1.opExtrude","SWEPT_EDGE",EDGE,{"disambiguationData":[OSD([sQuery(id+"F0.wireOp",EDGE,"E7.32.0"),sQuery(id+"F0.wireOp",EDGE,"E7.32.1")])]});
            var Q50;
            Q50=makeQuery(id+"F1.opExtrude","SWEPT_EDGE",EDGE,{"disambiguationData":[OSD([sQuery(id+"F0.wireOp",EDGE,"E0"),sQuery(id+"F0.wireOp",EDGE,"E7.32.1")])]});
            var Q51;
            Q51=makeQuery(id+"F1.opExtrude","SWEPT_EDGE",EDGE,{"disambiguationData":[OSD([sQuery(id+"F0.wireOp",EDGE,"E0"),sQuery(id+"F0.wireOp",EDGE,"E7.31.0")])]});
            var Q52;
            Q52=makeQuery(id+"F1.opExtrude","SWEPT_EDGE",EDGE,{"disambiguationData":[OSD([sQuery(id+"F0.wireOp",EDGE,"E7.31.0"),sQuery(id+"F0.wireOp",EDGE,"E7.31.1")])]});
            var Q53;
            Q53=makeQuery(id+"F1.opExtrude","SWEPT_EDGE",EDGE,{"disambiguationData":[OSD([sQuery(id+"F0.wireOp",EDGE,"E0"),sQuery(id+"F0.wireOp",EDGE,"E7.33.1")])]});
            var Q54;
            Q54=makeQuery(id+"F1.opExtrude","SWEPT_EDGE",EDGE,{"disambiguationData":[OSD([sQuery(id+"F0.wireOp",EDGE,"E0"),sQuery(id+"F0.wireOp",EDGE,"E7.31.1")])]});
            var Q55;
            Q55=makeQuery(id+"F1.opExtrude","SWEPT_EDGE",EDGE,{"disambiguationData":[OSD([sQuery(id+"F0.wireOp",EDGE,"E0"),sQuery(id+"F0.wireOp",EDGE,"E7.30.0")])]});
            var Q56;
            Q56=makeQuery(id+"F1.opExtrude","SWEPT_EDGE",EDGE,{"disambiguationData":[OSD([sQuery(id+"F0.wireOp",EDGE,"E7.30.0"),sQuery(id+"F0.wireOp",EDGE,"E7.30.1")])]});
            var Q57;
            Q57=makeQuery(id+"F1.opExtrude","SWEPT_EDGE",EDGE,{"disambiguationData":[OSD([sQuery(id+"F0.wireOp",EDGE,"E0"),sQuery(id+"F0.wireOp",EDGE,"E7.30.1")])]});
            var Q58;
            Q58=makeQuery(id+"F1.opExtrude","SWEPT_EDGE",EDGE,{"disambiguationData":[OSD([sQuery(id+"F0.wireOp",EDGE,"E0"),sQuery(id+"F0.wireOp",EDGE,"E7.29.0")])]});
            var Q59;
            Q59=makeQuery(id+"F1.opExtrude","SWEPT_EDGE",EDGE,{"disambiguationData":[OSD([sQuery(id+"F0.wireOp",EDGE,"E7.29.0"),sQuery(id+"F0.wireOp",EDGE,"E7.29.1")])]});
            var Q60;
            Q60=makeQuery(id+"F1.opExtrude","SWEPT_EDGE",EDGE,{"disambiguationData":[OSD([sQuery(id+"F0.wireOp",EDGE,"E0"),sQuery(id+"F0.wireOp",EDGE,"E7.29.1")])]});
            var Q61;
            Q61=makeQuery(id+"F1.opExtrude","SWEPT_EDGE",EDGE,{"disambiguationData":[OSD([sQuery(id+"F0.wireOp",EDGE,"E0"),sQuery(id+"F0.wireOp",EDGE,"E7.28.0")])]});
            var Q62;
            Q62=makeQuery(id+"F1.opExtrude","SWEPT_EDGE",EDGE,{"disambiguationData":[OSD([sQuery(id+"F0.wireOp",EDGE,"E7.28.0"),sQuery(id+"F0.wireOp",EDGE,"E7.28.1")])]});
            var Q63;
            Q63=makeQuery(id+"F1.opExtrude","SWEPT_EDGE",EDGE,{"disambiguationData":[OSD([sQuery(id+"F0.wireOp",EDGE,"E0"),sQuery(id+"F0.wireOp",EDGE,"E7.28.1")])]});
            var Q64;
            Q64=makeQuery(id+"F1.opExtrude","SWEPT_EDGE",EDGE,{"disambiguationData":[OSD([sQuery(id+"F0.wireOp",EDGE,"E0"),sQuery(id+"F0.wireOp",EDGE,"E7.27.0")])]});
            var Q65;
            Q65=makeQuery(id+"F1.opExtrude","SWEPT_EDGE",EDGE,{"disambiguationData":[OSD([sQuery(id+"F0.wireOp",EDGE,"E7.27.0"),sQuery(id+"F0.wireOp",EDGE,"E7.27.1")])]});
            var Q66;
            Q66=makeQuery(id+"F1.opExtrude","SWEPT_EDGE",EDGE,{"disambiguationData":[OSD([sQuery(id+"F0.wireOp",EDGE,"E0"),sQuery(id+"F0.wireOp",EDGE,"E7.27.1")])]});
            var Q67;
            Q67=makeQuery(id+"F1.opExtrude","SWEPT_EDGE",EDGE,{"disambiguationData":[OSD([sQuery(id+"F0.wireOp",EDGE,"E0"),sQuery(id+"F0.wireOp",EDGE,"E7.26.0")])]});
            var Q68;
            Q68=makeQuery(id+"F1.opExtrude","SWEPT_EDGE",EDGE,{"disambiguationData":[OSD([sQuery(id+"F0.wireOp",EDGE,"E7.26.0"),sQuery(id+"F0.wireOp",EDGE,"E7.26.1")])]});
            var Q69;
            Q69=makeQuery(id+"F1.opExtrude","SWEPT_EDGE",EDGE,{"disambiguationData":[OSD([sQuery(id+"F0.wireOp",EDGE,"E0"),sQuery(id+"F0.wireOp",EDGE,"E7.26.1")])]});
            var Q70;
            Q70=makeQuery(id+"F1.opExtrude","SWEPT_EDGE",EDGE,{"disambiguationData":[OSD([sQuery(id+"F0.wireOp",EDGE,"E0"),sQuery(id+"F0.wireOp",EDGE,"E7.25.0")])]});
            var Q71;
            Q71=makeQuery(id+"F1.opExtrude","SWEPT_EDGE",EDGE,{"disambiguationData":[OSD([sQuery(id+"F0.wireOp",EDGE,"E7.25.0"),sQuery(id+"F0.wireOp",EDGE,"E7.25.1")])]});
            var Q72;
            Q72=makeQuery(id+"F1.opExtrude","SWEPT_EDGE",EDGE,{"disambiguationData":[OSD([sQuery(id+"F0.wireOp",EDGE,"E0"),sQuery(id+"F0.wireOp",EDGE,"E7.25.1")])]});
            var Q73;
            Q73=makeQuery(id+"F1.opExtrude","SWEPT_EDGE",EDGE,{"disambiguationData":[OSD([sQuery(id+"F0.wireOp",EDGE,"E0"),sQuery(id+"F0.wireOp",EDGE,"E7.24.0")])]});
            var Q74;
            Q74=makeQuery(id+"F1.opExtrude","SWEPT_EDGE",EDGE,{"disambiguationData":[OSD([sQuery(id+"F0.wireOp",EDGE,"E7.24.0"),sQuery(id+"F0.wireOp",EDGE,"E7.24.1")])]});
            var Q75;
            Q75=makeQuery(id+"F1.opExtrude","SWEPT_EDGE",EDGE,{"disambiguationData":[OSD([sQuery(id+"F0.wireOp",EDGE,"E0"),sQuery(id+"F0.wireOp",EDGE,"E7.24.1")])]});
            var Q76;
            Q76=makeQuery(id+"F1.opExtrude","SWEPT_EDGE",EDGE,{"disambiguationData":[OSD([sQuery(id+"F0.wireOp",EDGE,"E0"),sQuery(id+"F0.wireOp",EDGE,"E7.23.0")])]});
            var Q77;
            Q77=makeQuery(id+"F1.opExtrude","SWEPT_EDGE",EDGE,{"disambiguationData":[OSD([sQuery(id+"F0.wireOp",EDGE,"E0"),sQuery(id+"F0.wireOp",EDGE,"E7.23.1")])]});
            var Q78;
            Q78=makeQuery(id+"F1.opExtrude","SWEPT_EDGE",EDGE,{"disambiguationData":[OSD([sQuery(id+"F0.wireOp",EDGE,"E0"),sQuery(id+"F0.wireOp",EDGE,"E7.22.0")])]});
            var Q79;
            Q79=makeQuery(id+"F1.opExtrude","SWEPT_EDGE",EDGE,{"disambiguationData":[OSD([sQuery(id+"F0.wireOp",EDGE,"E7.22.0"),sQuery(id+"F0.wireOp",EDGE,"E7.22.1")])]});
            var Q80;
            Q80=makeQuery(id+"F1.opExtrude","SWEPT_EDGE",EDGE,{"disambiguationData":[OSD([sQuery(id+"F0.wireOp",EDGE,"E0"),sQuery(id+"F0.wireOp",EDGE,"E7.22.1")])]});
            var Q81;
            Q81=makeQuery(id+"F1.opExtrude","SWEPT_EDGE",EDGE,{"disambiguationData":[OSD([sQuery(id+"F0.wireOp",EDGE,"E0"),sQuery(id+"F0.wireOp",EDGE,"E7.21.0")])]});
            var Q82;
            Q82=makeQuery(id+"F1.opExtrude","SWEPT_EDGE",EDGE,{"disambiguationData":[OSD([sQuery(id+"F0.wireOp",EDGE,"E7.21.0"),sQuery(id+"F0.wireOp",EDGE,"E7.21.1")])]});
            var Q83;
            Q83=makeQuery(id+"F1.opExtrude","SWEPT_EDGE",EDGE,{"disambiguationData":[OSD([sQuery(id+"F0.wireOp",EDGE,"E0"),sQuery(id+"F0.wireOp",EDGE,"E7.21.1")])]});
            var Q84;
            Q84=makeQuery(id+"F1.opExtrude","SWEPT_EDGE",EDGE,{"disambiguationData":[OSD([sQuery(id+"F0.wireOp",EDGE,"E7.23.0"),sQuery(id+"F0.wireOp",EDGE,"E7.23.1")])]});
            var Q85;
            Q85=makeQuery(id+"F1.opExtrude","SWEPT_EDGE",EDGE,{"disambiguationData":[OSD([sQuery(id+"F0.wireOp",EDGE,"E7.20.0"),sQuery(id+"F0.wireOp",EDGE,"E7.20.1")])]});
            var Q86;
            Q86=makeQuery(id+"F1.opExtrude","SWEPT_EDGE",EDGE,{"disambiguationData":[OSD([sQuery(id+"F0.wireOp",EDGE,"E0"),sQuery(id+"F0.wireOp",EDGE,"E7.20.1")])]});
            var Q87;
            Q87=makeQuery(id+"F1.opExtrude","SWEPT_EDGE",EDGE,{"disambiguationData":[OSD([sQuery(id+"F0.wireOp",EDGE,"E0"),sQuery(id+"F0.wireOp",EDGE,"E7.20.0")])]});
            var Q88;
            Q88=makeQuery(id+"F1.opExtrude","SWEPT_EDGE",EDGE,{"disambiguationData":[OSD([sQuery(id+"F0.wireOp",EDGE,"E0"),sQuery(id+"F0.wireOp",EDGE,"E7.19.0")])]});
            var Q89;
            Q89=makeQuery(id+"F1.opExtrude","SWEPT_EDGE",EDGE,{"disambiguationData":[OSD([sQuery(id+"F0.wireOp",EDGE,"E7.19.0"),sQuery(id+"F0.wireOp",EDGE,"E7.19.1")])]});
            var Q90;
            Q90=makeQuery(id+"F1.opExtrude","SWEPT_EDGE",EDGE,{"disambiguationData":[OSD([sQuery(id+"F0.wireOp",EDGE,"E0"),sQuery(id+"F0.wireOp",EDGE,"E7.19.1")])]});
            var Q91;
            Q91=makeQuery(id+"F1.opExtrude","SWEPT_EDGE",EDGE,{"disambiguationData":[OSD([sQuery(id+"F0.wireOp",EDGE,"E0"),sQuery(id+"F0.wireOp",EDGE,"E7.18.0")])]});
            var Q92;
            Q92=makeQuery(id+"F1.opExtrude","SWEPT_EDGE",EDGE,{"disambiguationData":[OSD([sQuery(id+"F0.wireOp",EDGE,"E7.18.0"),sQuery(id+"F0.wireOp",EDGE,"E7.18.1")])]});
            var Q93;
            Q93=makeQuery(id+"F1.opExtrude","SWEPT_EDGE",EDGE,{"disambiguationData":[OSD([sQuery(id+"F0.wireOp",EDGE,"E0"),sQuery(id+"F0.wireOp",EDGE,"E7.18.1")])]});
            var Q94;
            Q94=makeQuery(id+"F1.opExtrude","SWEPT_EDGE",EDGE,{"disambiguationData":[OSD([sQuery(id+"F0.wireOp",EDGE,"E0"),sQuery(id+"F0.wireOp",EDGE,"E7.17.0")])]});
            var Q95;
            Q95=makeQuery(id+"F1.opExtrude","SWEPT_EDGE",EDGE,{"disambiguationData":[OSD([sQuery(id+"F0.wireOp",EDGE,"E7.17.0"),sQuery(id+"F0.wireOp",EDGE,"E7.17.1")])]});
            var Q96;
            Q96=makeQuery(id+"F1.opExtrude","SWEPT_EDGE",EDGE,{"disambiguationData":[OSD([sQuery(id+"F0.wireOp",EDGE,"E0"),sQuery(id+"F0.wireOp",EDGE,"E7.17.1")])]});
            var Q97;
            Q97=makeQuery(id+"F1.opExtrude","SWEPT_EDGE",EDGE,{"disambiguationData":[OSD([sQuery(id+"F0.wireOp",EDGE,"E0"),sQuery(id+"F0.wireOp",EDGE,"E7.16.0")])]});
            var Q98;
            Q98=makeQuery(id+"F1.opExtrude","SWEPT_EDGE",EDGE,{"disambiguationData":[OSD([sQuery(id+"F0.wireOp",EDGE,"E7.16.0"),sQuery(id+"F0.wireOp",EDGE,"E7.16.1")])]});
            var Q99;
            Q99=makeQuery(id+"F1.opExtrude","SWEPT_EDGE",EDGE,{"disambiguationData":[OSD([sQuery(id+"F0.wireOp",EDGE,"E0"),sQuery(id+"F0.wireOp",EDGE,"E7.16.1")])]});
            var Q100;
            Q100=makeQuery(id+"F1.opExtrude","SWEPT_EDGE",EDGE,{"disambiguationData":[OSD([sQuery(id+"F0.wireOp",EDGE,"E0"),sQuery(id+"F0.wireOp",EDGE,"E7.15.0")])]});
            var Q101;
            Q101=makeQuery(id+"F1.opExtrude","SWEPT_EDGE",EDGE,{"disambiguationData":[OSD([sQuery(id+"F0.wireOp",EDGE,"E7.15.0"),sQuery(id+"F0.wireOp",EDGE,"E7.15.1")])]});
            var Q102;
            Q102=makeQuery(id+"F1.opExtrude","SWEPT_EDGE",EDGE,{"disambiguationData":[OSD([sQuery(id+"F0.wireOp",EDGE,"E0"),sQuery(id+"F0.wireOp",EDGE,"E7.15.1")])]});
            var Q103;
            Q103=makeQuery(id+"F1.opExtrude","SWEPT_EDGE",EDGE,{"disambiguationData":[OSD([sQuery(id+"F0.wireOp",EDGE,"E0"),sQuery(id+"F0.wireOp",EDGE,"E7.14.0")])]});
            var Q104;
            Q104=makeQuery(id+"F1.opExtrude","SWEPT_EDGE",EDGE,{"disambiguationData":[OSD([sQuery(id+"F0.wireOp",EDGE,"E7.14.0"),sQuery(id+"F0.wireOp",EDGE,"E7.14.1")])]});
            var Q105;
            Q105=makeQuery(id+"F1.opExtrude","SWEPT_EDGE",EDGE,{"disambiguationData":[OSD([sQuery(id+"F0.wireOp",EDGE,"E0"),sQuery(id+"F0.wireOp",EDGE,"E7.14.1")])]});
            var Q106;
            Q106=makeQuery(id+"F1.opExtrude","SWEPT_EDGE",EDGE,{"disambiguationData":[OSD([sQuery(id+"F0.wireOp",EDGE,"E0"),sQuery(id+"F0.wireOp",EDGE,"E7.13.0")])]});
            var Q107;
            Q107=makeQuery(id+"F1.opExtrude","SWEPT_EDGE",EDGE,{"disambiguationData":[OSD([sQuery(id+"F0.wireOp",EDGE,"E7.13.0"),sQuery(id+"F0.wireOp",EDGE,"E7.13.1")])]});
            var Q108;
            Q108=makeQuery(id+"F1.opExtrude","SWEPT_EDGE",EDGE,{"disambiguationData":[OSD([sQuery(id+"F0.wireOp",EDGE,"E7.12.0"),sQuery(id+"F0.wireOp",EDGE,"E7.12.1")])]});
            var Q109;
            Q109=makeQuery(id+"F1.opExtrude","SWEPT_EDGE",EDGE,{"disambiguationData":[OSD([sQuery(id+"F0.wireOp",EDGE,"E0"),sQuery(id+"F0.wireOp",EDGE,"E7.12.1")])]});
            var Q110;
            Q110=makeQuery(id+"F1.opExtrude","SWEPT_EDGE",EDGE,{"disambiguationData":[OSD([sQuery(id+"F0.wireOp",EDGE,"E0"),sQuery(id+"F0.wireOp",EDGE,"E7.13.1")])]});
            var Q111;
            Q111=makeQuery(id+"F1.opExtrude","SWEPT_EDGE",EDGE,{"disambiguationData":[OSD([sQuery(id+"F0.wireOp",EDGE,"E0"),sQuery(id+"F0.wireOp",EDGE,"E7.12.0")])]});
            var Q112;
            Q112=makeQuery(id+"F1.opExtrude","SWEPT_EDGE",EDGE,{"disambiguationData":[OSD([sQuery(id+"F0.wireOp",EDGE,"E7.11.0"),sQuery(id+"F0.wireOp",EDGE,"E7.11.1")])]});
            var Q113;
            Q113=makeQuery(id+"F1.opExtrude","SWEPT_EDGE",EDGE,{"disambiguationData":[OSD([sQuery(id+"F0.wireOp",EDGE,"E0"),sQuery(id+"F0.wireOp",EDGE,"E7.11.1")])]});
            var Q114;
            Q114=makeQuery(id+"F1.opExtrude","SWEPT_EDGE",EDGE,{"disambiguationData":[OSD([sQuery(id+"F0.wireOp",EDGE,"E0"),sQuery(id+"F0.wireOp",EDGE,"E7.10.0")])]});
            var Q115;
            Q115=makeQuery(id+"F1.opExtrude","SWEPT_EDGE",EDGE,{"disambiguationData":[OSD([sQuery(id+"F0.wireOp",EDGE,"E7.10.0"),sQuery(id+"F0.wireOp",EDGE,"E7.10.1")])]});
            var Q116;
            Q116=makeQuery(id+"F1.opExtrude","SWEPT_EDGE",EDGE,{"disambiguationData":[OSD([sQuery(id+"F0.wireOp",EDGE,"E0"),sQuery(id+"F0.wireOp",EDGE,"E7.10.1")])]});
            var Q117;
            Q117=makeQuery(id+"F1.opExtrude","SWEPT_EDGE",EDGE,{"disambiguationData":[OSD([sQuery(id+"F0.wireOp",EDGE,"E0"),sQuery(id+"F0.wireOp",EDGE,"E7.9.0")])]});
            var Q118;
            Q118=makeQuery(id+"F1.opExtrude","SWEPT_EDGE",EDGE,{"disambiguationData":[OSD([sQuery(id+"F0.wireOp",EDGE,"E0"),sQuery(id+"F0.wireOp",EDGE,"E7.11.0")])]});
            var Q119;
            Q119=makeQuery(id+"F1.opExtrude","SWEPT_EDGE",EDGE,{"disambiguationData":[OSD([sQuery(id+"F0.wireOp",EDGE,"E7.9.0"),sQuery(id+"F0.wireOp",EDGE,"E7.9.1")])]});
            var Q120;
            Q120=makeQuery(id+"F1.opExtrude","SWEPT_EDGE",EDGE,{"disambiguationData":[OSD([sQuery(id+"F0.wireOp",EDGE,"E0"),sQuery(id+"F0.wireOp",EDGE,"E7.9.1")])]});
            var Q121;
            Q121=makeQuery(id+"F1.opExtrude","SWEPT_EDGE",EDGE,{"disambiguationData":[OSD([sQuery(id+"F0.wireOp",EDGE,"E0"),sQuery(id+"F0.wireOp",EDGE,"E7.8.0")])]});
            var Q122;
            Q122=makeQuery(id+"F1.opExtrude","SWEPT_EDGE",EDGE,{"disambiguationData":[OSD([sQuery(id+"F0.wireOp",EDGE,"E0"),sQuery(id+"F0.wireOp",EDGE,"E7.8.1")])]});
            var Q123;
            Q123=makeQuery(id+"F1.opExtrude","SWEPT_EDGE",EDGE,{"disambiguationData":[OSD([sQuery(id+"F0.wireOp",EDGE,"E0"),sQuery(id+"F0.wireOp",EDGE,"E7.7.0")])]});
            var Q124;
            Q124=makeQuery(id+"F1.opExtrude","SWEPT_EDGE",EDGE,{"disambiguationData":[OSD([sQuery(id+"F0.wireOp",EDGE,"E0"),sQuery(id+"F0.wireOp",EDGE,"E7.6.0")])]});
            var Q125;
            Q125=makeQuery(id+"F1.opExtrude","SWEPT_EDGE",EDGE,{"disambiguationData":[OSD([sQuery(id+"F0.wireOp",EDGE,"E7.6.0"),sQuery(id+"F0.wireOp",EDGE,"E7.6.1")])]});
            var Q126;
            Q126=makeQuery(id+"F1.opExtrude","SWEPT_EDGE",EDGE,{"disambiguationData":[OSD([sQuery(id+"F0.wireOp",EDGE,"E0"),sQuery(id+"F0.wireOp",EDGE,"E7.5.0")])]});
            var Q127;
            Q127=makeQuery(id+"F1.opExtrude","SWEPT_EDGE",EDGE,{"disambiguationData":[OSD([sQuery(id+"F0.wireOp",EDGE,"E7.5.0"),sQuery(id+"F0.wireOp",EDGE,"E7.5.1")])]});
            var Q128;
            Q128=makeQuery(id+"F1.opExtrude","SWEPT_EDGE",EDGE,{"disambiguationData":[OSD([sQuery(id+"F0.wireOp",EDGE,"E0"),sQuery(id+"F0.wireOp",EDGE,"E7.4.0")])]});
            var Q129;
            Q129=makeQuery(id+"F1.opExtrude","SWEPT_EDGE",EDGE,{"disambiguationData":[OSD([sQuery(id+"F0.wireOp",EDGE,"E7.4.0"),sQuery(id+"F0.wireOp",EDGE,"E7.4.1")])]});
            var Q130;
            Q130=makeQuery(id+"F1.opExtrude","SWEPT_EDGE",EDGE,{"disambiguationData":[OSD([sQuery(id+"F0.wireOp",EDGE,"E0"),sQuery(id+"F0.wireOp",EDGE,"E7.3.0")])]});
            var Q131;
            Q131=makeQuery(id+"F1.opExtrude","SWEPT_EDGE",EDGE,{"disambiguationData":[OSD([sQuery(id+"F0.wireOp",EDGE,"E7.3.0"),sQuery(id+"F0.wireOp",EDGE,"E7.3.1")])]});
            var Q132;
            Q132=makeQuery(id+"F1.opExtrude","SWEPT_EDGE",EDGE,{"disambiguationData":[OSD([sQuery(id+"F0.wireOp",EDGE,"E0"),sQuery(id+"F0.wireOp",EDGE,"E7.2.0")])]});
            var Q133;
            Q133=makeQuery(id+"F1.opExtrude","SWEPT_EDGE",EDGE,{"disambiguationData":[OSD([sQuery(id+"F0.wireOp",EDGE,"E7.2.0"),sQuery(id+"F0.wireOp",EDGE,"E7.2.1")])]});
            var Q134;
            Q134=makeQuery(id+"F1.opExtrude","SWEPT_EDGE",EDGE,{"disambiguationData":[OSD([sQuery(id+"F0.wireOp",EDGE,"E0"),sQuery(id+"F0.wireOp",EDGE,"E7.2.1")])]});
            var Q135;
            Q135=makeQuery(id+"F1.opExtrude","SWEPT_EDGE",EDGE,{"disambiguationData":[OSD([sQuery(id+"F0.wireOp",EDGE,"E0"),sQuery(id+"F0.wireOp",EDGE,"E7.1.0")])]});
            var Q136;
            Q136=makeQuery(id+"F1.opExtrude","SWEPT_EDGE",EDGE,{"disambiguationData":[OSD([sQuery(id+"F0.wireOp",EDGE,"E0"),sQuery(id+"F0.wireOp",EDGE,"E7.3.1")])]});
            fillet(context, id + "F2", {"entities" : qUnion([Q0, Q1, Q2, Q3, Q4, Q5, Q6, Q7, Q8, Q9, Q10, Q11, Q12, Q13, Q14, Q15, Q16, Q17, Q18, Q19, Q20, Q21, Q22, Q23, Q24, Q25, Q26, Q27, Q28, Q29, Q30, Q31, Q32, Q33, Q34, Q35, Q36, Q37, Q38, Q39, Q40, Q41, Q42, Q43, Q44, Q45, Q46, Q47, Q48, Q49, Q50, Q51, Q52, Q53, Q54, Q55, Q56, Q57, Q58, Q59, Q60, Q61, Q62, Q63, Q64, Q65, Q66, Q67, Q68, Q69, Q70, Q71, Q72, Q73, Q74, Q75, Q76, Q77, Q78, Q79, Q80, Q81, Q82, Q83, Q84, Q85, Q86, Q87, Q88, Q89, Q90, Q91, Q92, Q93, Q94, Q95, Q96, Q97, Q98, Q99, Q100, Q101, Q102, Q103, Q104, Q105, Q106, Q107, Q108, Q109, Q110, Q111, Q112, Q113, Q114, Q115, Q116, Q117, Q118, Q119, Q120, Q121, Q122, Q123, Q124, Q125, Q126, Q127, Q128, Q129, Q130, Q131, Q132, Q133, Q134, Q135, Q136]), "radius" : 0.1 * mm, "tangentPropagation" : true, "allowEdgeOverflow" : false});
        }
    });
